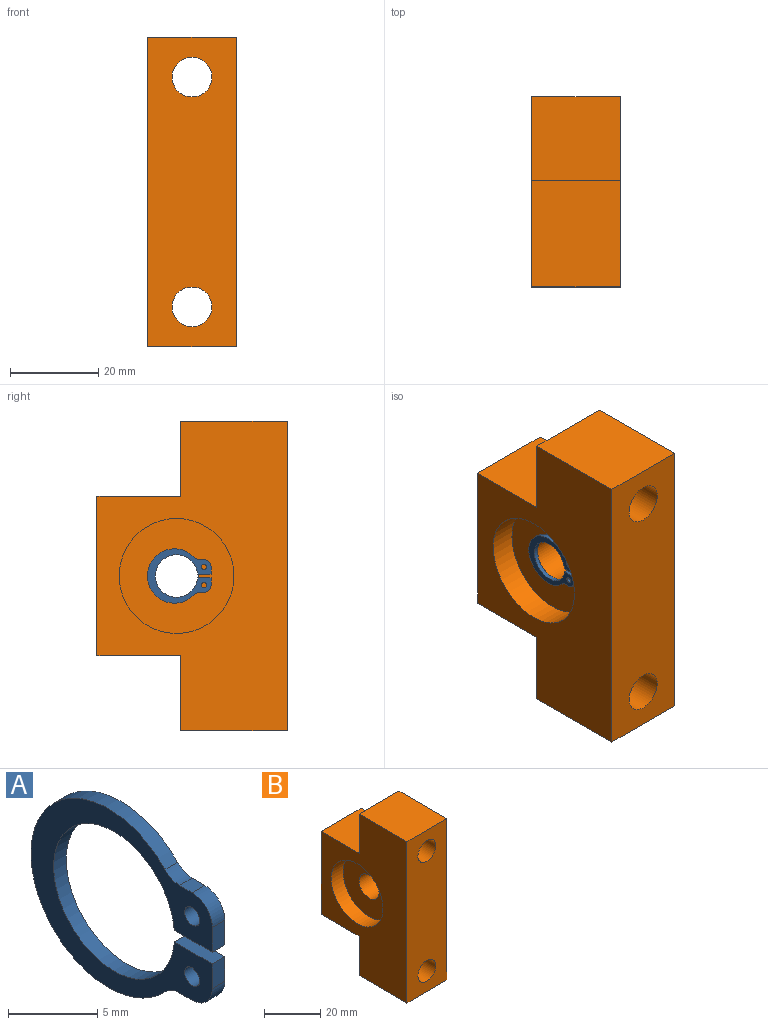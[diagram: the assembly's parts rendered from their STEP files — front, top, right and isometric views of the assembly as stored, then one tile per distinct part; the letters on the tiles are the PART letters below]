
ASSEMBLY  parts=2 mates=1
PART A: 16 faces, bbox 1x14.4x12.3 mm
  f0: cylinder r=1.6mm len=1.17mm, axis (-1,0,0), area 1.3mm2, adj f1,f13,f14,f15
  f1: cylinder r=6.15mm len=12.3mm, axis (-1,0,0), area 29.4mm2, adj f0,f2,f14,f15
  f2: cylinder r=1.6mm len=1.17mm, axis (-1,0,0), area 1.3mm2, adj f1,f3,f14,f15
  f3: plane 1x1mm, normal (0,0,1), area 1mm2, adj f2,f4,f14,f15
  f4: cylinder r=1.6mm len=1.6mm, axis (-1,0,0), area 2.5mm2, adj f3,f5,f14,f15
  f5: plane 1.7x1mm, normal (0,-1,0), area 1.7mm2, adj f4,f7,f14,f15
  f6: cylinder r=0.6mm len=1.2mm, axis (-1,0,0), area 3.8mm2, adj f14,f15
  f7: plane 3.02x1mm, normal (0,0,-1), area 3mm2, adj f5,f8,f14,f15
  f8: cylinder r=4.8mm len=9.6mm, axis (-1,0,0), area 29.4mm2, adj f7,f10,f14,f15
  f9: cylinder r=0.6mm len=1.2mm, axis (-1,0,0), area 3.8mm2, adj f14,f15
  f10: plane 3.02x1mm, normal (0,0,1), area 3mm2, adj f8,f11,f14,f15
  f11: plane 1.7x1mm, normal (0,-1,0), area 1.7mm2, adj f10,f12,f14,f15
  f12: cylinder r=1.6mm len=1.6mm, axis (-1,0,0), area 2.5mm2, adj f11,f13,f14,f15
  f13: plane 1x1mm, normal (0,0,-1), area 1mm2, adj f0,f12,f14,f15
  f14: plane 14.4x12.3mm, normal (1,0,0), area 59.3mm2, adj f0,f1,f2,f3,f4,f5,f6,f7
  f15: plane 14.4x12.3mm, normal (-1,0,0), area 59.3mm2, adj f0,f1,f2,f3,f4,f5,f6,f7
PART B: 17 faces, bbox 20x43x70 mm
  f0: cylinder r=13mm len=26mm, axis (1,0,0), area 490.1mm2, adj f10,f13
  f1: plane 70x20mm, normal (0,-1,0), area 1272.8mm2, adj f4,f5,f6,f7,f10,f11
  f2: cylinder r=5mm len=10mm, axis (1,0,0), area 251.3mm2, adj f13,f14
  f3: cylinder r=13mm len=26mm, axis (1,0,0), area 490.1mm2, adj f7,f14
  f4: cylinder r=4.5mm len=24mm, axis (0,1,0), area 678.6mm2, adj f1,f15
  f5: cylinder r=4.5mm len=24mm, axis (0,-1,0), area 678.6mm2, adj f1,f16
  f6: plane 24x20mm, normal (0,0,-1), area 480mm2, adj f1,f7,f10,f16
  f7: plane 70x43mm, normal (1,0,0), area 1833.1mm2, adj f1,f3,f6,f8,f9,f11,f12,f15
  f8: plane 20x19mm, normal (0,0,-1), area 380mm2, adj f7,f9,f10,f16
  f9: plane 36x20mm, normal (0,1,0), area 720mm2, adj f7,f8,f10,f12
  f10: plane 70x43mm, normal (-1,0,0), area 1833.1mm2, adj f0,f1,f6,f8,f9,f11,f12,f15
  f11: plane 24x20mm, normal (0,0,1), area 480mm2, adj f1,f7,f10,f15
  f12: plane 20x19mm, normal (0,0,1), area 380mm2, adj f7,f9,f10,f15
  f13: plane 26x26mm, normal (-1,0,0), area 452.4mm2, adj f0,f2
  f14: plane 26x26mm, normal (1,0,0), area 452.4mm2, adj f2,f3
  f15: plane 20x17mm, normal (0,1,0), area 276.4mm2, adj f4,f7,f10,f11,f12
  f16: plane 20x17mm, normal (0,1,0), area 276.4mm2, adj f5,f6,f7,f8,f10
PLACE A t=(-17.39,-18.43,14.3)mm
PLACE B t=(-12.89,-43.43,14.3)mm
MATE revolute A.f8 <-> B.f0  axis (1,0,0) through (-16.89,-18.43,14.3)mm
